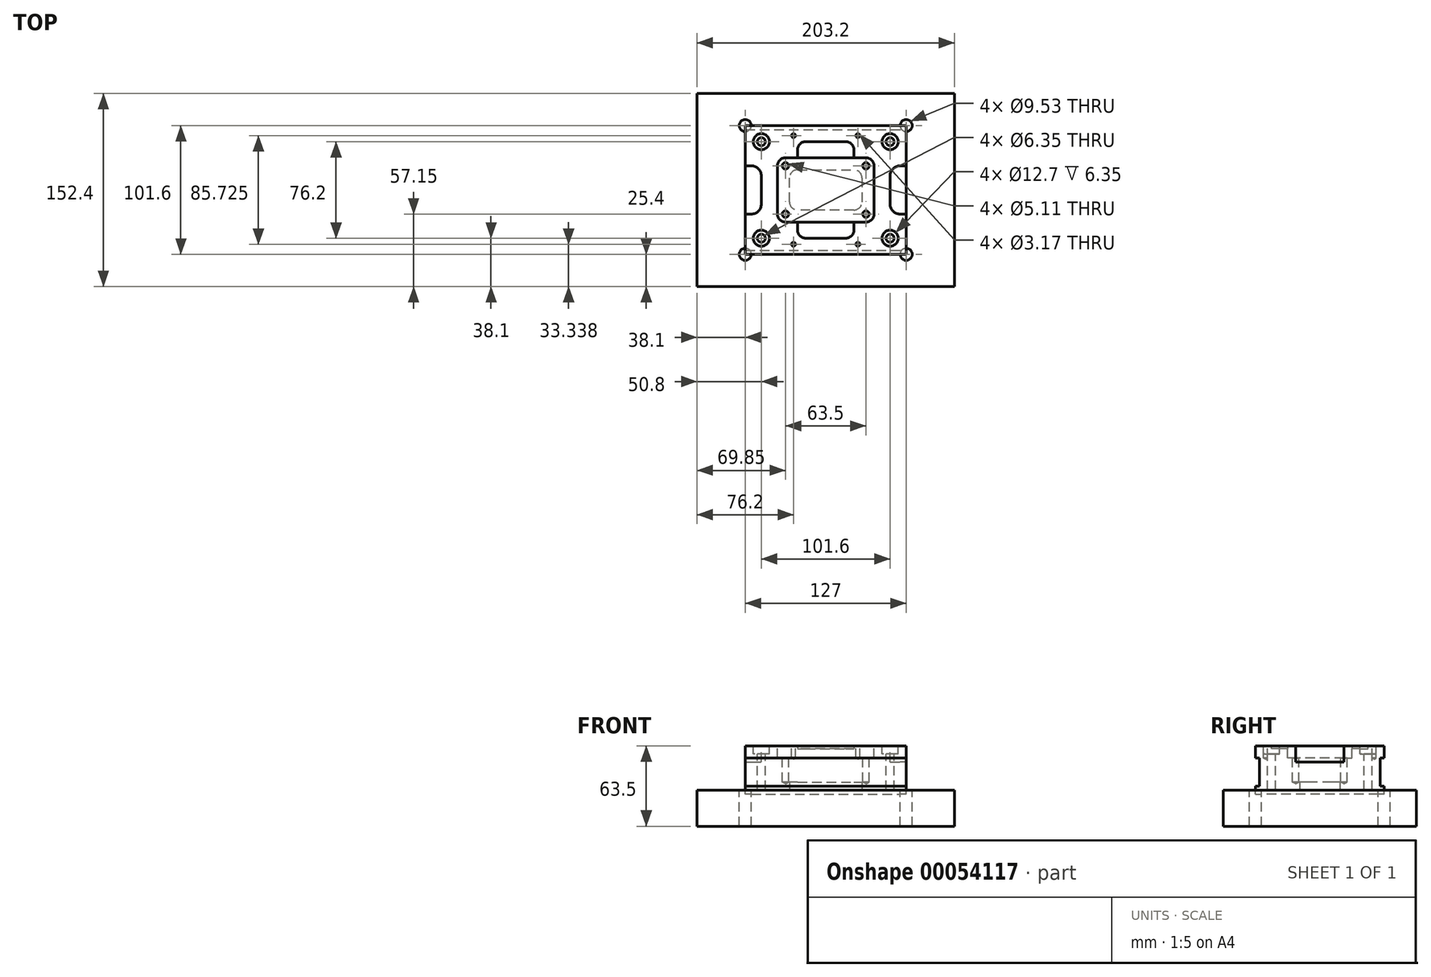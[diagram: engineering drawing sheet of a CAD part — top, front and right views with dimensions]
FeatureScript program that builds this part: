
annotation { "Feature Type Name" : "Feature", "Feature Type Description" : "" }
export const myFeature = defineFeature(function(context is Context, id is Id, definition is map)
    precondition{}
    {
        {
            var Q0;
            Q0=qCreatedBy(makeId("Top.planeOp"),FACE);
            var sketch = newSketch(context, id + "F0", { "sketchPlane" : qUnion([Q0])});
            skLineSegment(sketch, "E0.rect.bottom", {"start": v(-63.5, 50.8) * mm, "end": v(63.5, 50.8) * mm});
            skLineSegment(sketch, "E0.rect.top", {"start": v(-63.5, -50.8) * mm, "end": v(63.5, -50.8) * mm});
            skLineSegment(sketch, "E0.rect.left", {"start": v(-63.5, 50.8) * mm, "end": v(-63.5, -50.8) * mm});
            skLineSegment(sketch, "E0.rect.right", {"start": v(63.5, 50.8) * mm, "end": v(63.5, -50.8) * mm});
            skPoint(sketch, "E0.rect.middle", {"position": v(0, 0) * mm});
            skSolve(sketch);
        }
        {
            var Q0;
            Q0=makeQuery(id+"F0.imprint","IMPRINT",FACE,{"disambiguationData":[TD([[makeQuery(id+"F0.imprint","IMPRINT",EDGE,{"derivedFrom":sQuery(id+"F0.wireOp",EDGE,"E0.rect.bottom")}),-1.0]])]});
            extrude(context, id + "F1", {"entities" : qUnion([Q0]), "depth" : 38.1 * mm});
        }
        {
            var Q0;
            Q0=makeQuery(id+"F1.opExtrude","CAP_FACE",FACE,{"disambiguationData":[OSD([sQuery(id+"F0.wireOp",EDGE,"E0.rect.bottom"),sQuery(id+"F0.wireOp",EDGE,"E0.rect.top"),sQuery(id+"F0.wireOp",EDGE,"E0.rect.left"),sQuery(id+"F0.wireOp",EDGE,"E0.rect.right")])],"isStart":false});
            var sketch = newSketch(context, id + "F2", { "sketchPlane" : qUnion([Q0])});
            skLineSegment(sketch, "E1.rect.bottom", {"start": v(-38.1, 25.4) * mm, "end": v(38.1, 25.4) * mm});
            skLineSegment(sketch, "E1.rect.top", {"start": v(-38.1, -25.4) * mm, "end": v(38.1, -25.4) * mm});
            skLineSegment(sketch, "E1.rect.left", {"start": v(-38.1, 25.4) * mm, "end": v(-38.1, -25.4) * mm});
            skLineSegment(sketch, "E1.rect.right", {"start": v(38.1, 25.4) * mm, "end": v(38.1, -25.4) * mm});
            skPoint(sketch, "E1.rect.middle", {"position": v(0, 0) * mm});
            skSolve(sketch);
        }
        {
            var Q0;
            Q0 = qSketchRegion(id + "F2", true);
            extrude(context, id + "F3", {"entities" : qUnion([Q0]), "operationType" : NewBodyOperationType.REMOVE, "oppositeDirection" : true, "depth" : 9.52 * mm});
        }
        {
            var Q0;
            Q0=makeQuery(id+"F3.boolean.opBoolean","COPY",EDGE,{"derivedFrom":makeQuery(id+"F3.opExtrude","SWEPT_EDGE",EDGE,{"disambiguationData":[OSD([sQuery(id+"F2.wireOp",EDGE,"E1.rect.bottom"),sQuery(id+"F2.wireOp",EDGE,"E1.rect.left")])]})});
            var Q1;
            Q1=makeQuery(id+"F3.boolean.opBoolean","COPY",EDGE,{"derivedFrom":makeQuery(id+"F3.opExtrude","SWEPT_EDGE",EDGE,{"disambiguationData":[OSD([sQuery(id+"F2.wireOp",EDGE,"E1.rect.bottom"),sQuery(id+"F2.wireOp",EDGE,"E1.rect.right")])]})});
            var Q2;
            Q2=makeQuery(id+"F3.boolean.opBoolean","COPY",EDGE,{"derivedFrom":makeQuery(id+"F3.opExtrude","SWEPT_EDGE",EDGE,{"disambiguationData":[OSD([sQuery(id+"F2.wireOp",EDGE,"E1.rect.top"),sQuery(id+"F2.wireOp",EDGE,"E1.rect.right")])]})});
            var Q3;
            Q3=makeQuery(id+"F3.boolean.opBoolean","COPY",EDGE,{"derivedFrom":makeQuery(id+"F3.opExtrude","SWEPT_EDGE",EDGE,{"disambiguationData":[OSD([sQuery(id+"F2.wireOp",EDGE,"E1.rect.top"),sQuery(id+"F2.wireOp",EDGE,"E1.rect.left")])]})});
            fillet(context, id + "F4", {"entities" : qUnion([Q0, Q1, Q2, Q3]), "radius" : 6.35 * mm, "tangentPropagation" : true, "allowEdgeOverflow" : false});
        }
        {
            var Q0;
            Q0=makeQuery(id+"F1.opExtrude","CAP_FACE",FACE,{"disambiguationData":[OSD([sQuery(id+"F0.wireOp",EDGE,"E0.rect.bottom"),sQuery(id+"F0.wireOp",EDGE,"E0.rect.top"),sQuery(id+"F0.wireOp",EDGE,"E0.rect.left"),sQuery(id+"F0.wireOp",EDGE,"E0.rect.right")])],"isStart":false});
            var sketch = newSketch(context, id + "F5", { "sketchPlane" : qUnion([Q0])});
            skPoint(sketch, "E2", {"position": v(50.8, 38.1) * mm});
            skPoint(sketch, "E3", {"position": v(50.8, -38.1) * mm});
            skPoint(sketch, "E4", {"position": v(-50.8, -38.1) * mm});
            skPoint(sketch, "E5", {"position": v(-50.8, 38.1) * mm});
            skSolve(sketch);
        }
        {
            var Q0;
            Q0=sQuery(id+"F5.wireOp",VERTEX,"E5");
            var Q1;
            Q1=sQuery(id+"F5.wireOp",VERTEX,"E2");
            var Q2;
            Q2=sQuery(id+"F5.wireOp",VERTEX,"E3");
            var Q3;
            Q3=sQuery(id+"F5.wireOp",VERTEX,"E4");
            var Q4;
            Q4=makeQuery(id+"F1.opExtrude","SWEPT_BODY",BODY,{"disambiguationData":[OSD([sQuery(id+"F0.wireOp",EDGE,"E0.rect.bottom"),sQuery(id+"F0.wireOp",EDGE,"E0.rect.top"),sQuery(id+"F0.wireOp",EDGE,"E0.rect.left"),sQuery(id+"F0.wireOp",EDGE,"E0.rect.right")])]});
            hole(context, id + "F6", {"style" : HoleStyle.C_BORE, "holeDiameter" : 6.35 * mm, "cBoreDiameter" : 12.7 * mm, "cBoreDepth" : 6.35 * mm, "endStyle" : HoleEndStyle.THROUGH, "locations" : qUnion([Q0, Q1, Q2, Q3]), "scope" : qUnion([Q4])});
        }
        {
            var Q0;
            Q0=makeQuery(id+"F1.opExtrude","SWEPT_FACE",FACE,{"disambiguationData":[OSD([sQuery(id+"F0.wireOp",EDGE,"E0.rect.right")])]});
            var sketch = newSketch(context, id + "F7", { "sketchPlane" : qUnion([Q0])});
            skLineSegment(sketch, "E6.bottom", {"start": v(-50.8, 28.57) * mm, "end": v(-47.62, 28.57) * mm});
            skLineSegment(sketch, "E6.top", {"start": v(-50.8, 6.35) * mm, "end": v(-47.62, 6.35) * mm});
            skLineSegment(sketch, "E6.left", {"start": v(-50.8, 28.57) * mm, "end": v(-50.8, 6.35) * mm});
            skLineSegment(sketch, "E6.right", {"start": v(-47.62, 28.57) * mm, "end": v(-47.62, 6.35) * mm});
            skLineSegment(sketch, "E7.bottom", {"start": v(50.8, 28.57) * mm, "end": v(47.63, 28.57) * mm});
            skLineSegment(sketch, "E7.top", {"start": v(50.8, 6.35) * mm, "end": v(47.63, 6.35) * mm});
            skLineSegment(sketch, "E7.left", {"start": v(50.8, 28.57) * mm, "end": v(50.8, 6.35) * mm});
            skLineSegment(sketch, "E7.right", {"start": v(47.63, 28.58) * mm, "end": v(47.63, 6.35) * mm});
            skSolve(sketch);
        }
        {
            var Q0;
            Q0 = qSketchRegion(id + "F7", true);
            extrude(context, id + "F8", {"entities" : qUnion([Q0]), "operationType" : NewBodyOperationType.REMOVE, "endBound" : BoundingType.THROUGH_ALL, "oppositeDirection" : true, "depth" : 25.4 * mm});
        }
        {
            var Q0;
            Q0=makeQuery(id+"F3.boolean.opBoolean","COPY",FACE,{"derivedFrom":makeQuery(id+"F3.opExtrude","CAP_FACE",FACE,{"disambiguationData":[OSD([sQuery(id+"F2.wireOp",EDGE,"E1.rect.bottom"),sQuery(id+"F2.wireOp",EDGE,"E1.rect.top"),sQuery(id+"F2.wireOp",EDGE,"E1.rect.left"),sQuery(id+"F2.wireOp",EDGE,"E1.rect.right")])],"isStart":false})});
            var sketch = newSketch(context, id + "F9", { "sketchPlane" : qUnion([Q0])});
            skPoint(sketch, "E8", {"position": v(-31.75, 19.05) * mm});
            skPoint(sketch, "E9", {"position": v(-31.75, -19.05) * mm});
            skPoint(sketch, "E10", {"position": v(31.75, 19.05) * mm});
            skPoint(sketch, "E11", {"position": v(31.75, -19.05) * mm});
            skSolve(sketch);
        }
        {
            var Q0;
            Q0=sQuery(id+"F9.wireOp",VERTEX,"E8");
            var Q1;
            Q1=sQuery(id+"F9.wireOp",VERTEX,"E9");
            var Q2;
            Q2=sQuery(id+"F9.wireOp",VERTEX,"E11");
            var Q3;
            Q3=sQuery(id+"F9.wireOp",VERTEX,"E10");
            var Q4;
            Q4=makeQuery(id+"F1.opExtrude","SWEPT_BODY",BODY,{"disambiguationData":[OSD([sQuery(id+"F0.wireOp",EDGE,"E0.rect.bottom"),sQuery(id+"F0.wireOp",EDGE,"E0.rect.top"),sQuery(id+"F0.wireOp",EDGE,"E0.rect.left"),sQuery(id+"F0.wireOp",EDGE,"E0.rect.right")])]});
            hole(context, id + "F10", {"style" : HoleStyle.SIMPLE, "holeDiameter" : 5.1 * mm, "endStyle" : HoleEndStyle.BLIND, "holeDepth" : 19.05 * mm, "locations" : qUnion([Q0, Q1, Q2, Q3]), "scope" : qUnion([Q4])});
        }
        {
            var Q0;
            Q0=makeQuery(id+"F1.opExtrude","CAP_FACE",FACE,{"disambiguationData":[OSD([sQuery(id+"F0.wireOp",EDGE,"E0.rect.bottom"),sQuery(id+"F0.wireOp",EDGE,"E0.rect.top"),sQuery(id+"F0.wireOp",EDGE,"E0.rect.left"),sQuery(id+"F0.wireOp",EDGE,"E0.rect.right")])],"isStart":false});
            var sketch = newSketch(context, id + "F11", { "sketchPlane" : qUnion([Q0])});
            skLineSegment(sketch, "E12.bottom", {"start": v(-63.5, 19.05) * mm, "end": v(-50.8, 19.05) * mm});
            skLineSegment(sketch, "E12.top", {"start": v(-63.5, -19.05) * mm, "end": v(-50.8, -19.05) * mm});
            skLineSegment(sketch, "E12.left", {"start": v(-63.5, 19.05) * mm, "end": v(-63.5, -19.05) * mm});
            skLineSegment(sketch, "E12.right", {"start": v(-50.8, 19.05) * mm, "end": v(-50.8, -19.05) * mm});
            skLineSegment(sketch, "E13.bottom", {"start": v(63.5, 19.05) * mm, "end": v(50.8, 19.05) * mm});
            skLineSegment(sketch, "E13.top", {"start": v(63.5, -19.05) * mm, "end": v(50.8, -19.05) * mm});
            skLineSegment(sketch, "E13.left", {"start": v(63.5, 19.05) * mm, "end": v(63.5, -19.05) * mm});
            skLineSegment(sketch, "E13.right", {"start": v(50.8, 19.05) * mm, "end": v(50.8, -19.05) * mm});
            skSolve(sketch);
        }
        {
            var Q0;
            Q0 = qSketchRegion(id + "F11", true);
            extrude(context, id + "F12", {"entities" : qUnion([Q0]), "operationType" : NewBodyOperationType.REMOVE, "oppositeDirection" : true, "depth" : 12.7 * mm});
        }
        {
            var Q0;
            Q0=makeQuery(id+"F12.boolean.opBoolean","COPY",EDGE,{"derivedFrom":makeQuery(id+"F12.opExtrude","SWEPT_EDGE",EDGE,{"disambiguationData":[OSD([sQuery(id+"F11.wireOp",EDGE,"E12.bottom"),sQuery(id+"F11.wireOp",EDGE,"E12.right")])]})});
            var Q1;
            Q1=makeQuery(id+"F12.boolean.opBoolean","COPY",EDGE,{"derivedFrom":makeQuery(id+"F12.opExtrude","SWEPT_EDGE",EDGE,{"disambiguationData":[OSD([sQuery(id+"F11.wireOp",EDGE,"E12.top"),sQuery(id+"F11.wireOp",EDGE,"E12.right")])]})});
            var Q2;
            Q2=makeQuery(id+"F12.boolean.opBoolean","COPY",EDGE,{"derivedFrom":makeQuery(id+"F12.opExtrude","SWEPT_EDGE",EDGE,{"disambiguationData":[OSD([sQuery(id+"F11.wireOp",EDGE,"E13.bottom"),sQuery(id+"F11.wireOp",EDGE,"E13.right")])]})});
            var Q3;
            Q3=makeQuery(id+"F12.boolean.opBoolean","COPY",EDGE,{"derivedFrom":makeQuery(id+"F12.opExtrude","SWEPT_EDGE",EDGE,{"disambiguationData":[OSD([sQuery(id+"F11.wireOp",EDGE,"E13.top"),sQuery(id+"F11.wireOp",EDGE,"E13.right")])]})});
            fillet(context, id + "F13", {"entities" : qUnion([Q0, Q1, Q2, Q3]), "radius" : 7.94 * mm, "tangentPropagation" : true, "allowEdgeOverflow" : false});
        }
        {
            var Q0;
            Q0=makeQuery(id+"F1.opExtrude","CAP_FACE",FACE,{"disambiguationData":[OSD([sQuery(id+"F0.wireOp",EDGE,"E0.rect.bottom"),sQuery(id+"F0.wireOp",EDGE,"E0.rect.top"),sQuery(id+"F0.wireOp",EDGE,"E0.rect.left"),sQuery(id+"F0.wireOp",EDGE,"E0.rect.right")])],"isStart":true});
            var sketch = newSketch(context, id + "F14", { "sketchPlane" : qUnion([Q0])});
            skLineSegment(sketch, "E14.0.0", {"start": v(31.75, -25.4) * mm, "end": v(-31.75, -25.4) * mm});
            skArc(sketch, "E14.0.1", {"start": v(-31.75, -25.4) * mm, "mid": v(-36.24, -23.54) * mm, "end": v(-38.1, -19.05) * mm});
            skLineSegment(sketch, "E14.0.2", {"start": v(-38.1, -19.05) * mm, "end": v(-38.1, 19.05) * mm});
            skArc(sketch, "E14.0.3", {"start": v(-38.1, 19.05) * mm, "mid": v(-36.24, 23.54) * mm, "end": v(-31.75, 25.4) * mm});
            skLineSegment(sketch, "E14.0.4", {"start": v(-31.75, 25.4) * mm, "end": v(31.75, 25.4) * mm});
            skArc(sketch, "E14.0.5", {"start": v(31.75, 25.4) * mm, "mid": v(36.24, 23.54) * mm, "end": v(38.1, 19.05) * mm});
            skLineSegment(sketch, "E14.0.6", {"start": v(38.1, 19.05) * mm, "end": v(38.1, -19.05) * mm});
            skArc(sketch, "E14.0.7", {"start": v(38.1, -19.05) * mm, "mid": v(36.24, -23.54) * mm, "end": v(31.75, -25.4) * mm});
            skSolve(sketch);
        }
        {
            var Q0;
            Q0 = qSketchRegion(id + "F14", true);
            extrude(context, id + "F15", {"entities" : qUnion([Q0]), "operationType" : NewBodyOperationType.REMOVE, "oppositeDirection" : true, "depth" : 3.17 * mm});
        }
        {
            var Q0;
            Q0=makeQuery(id+"F15.boolean.opBoolean","COPY",FACE,{"derivedFrom":makeQuery(id+"F15.opExtrude","CAP_FACE",FACE,{"disambiguationData":[OSD([sQuery(id+"F14.wireOp",EDGE,"E14.0.0"),sQuery(id+"F14.wireOp",EDGE,"E14.0.1"),sQuery(id+"F14.wireOp",EDGE,"E14.0.2"),sQuery(id+"F14.wireOp",EDGE,"E14.0.3"),sQuery(id+"F14.wireOp",EDGE,"E14.0.4"),sQuery(id+"F14.wireOp",EDGE,"E14.0.5"),sQuery(id+"F14.wireOp",EDGE,"E14.0.6"),sQuery(id+"F14.wireOp",EDGE,"E14.0.7")])],"isStart":false})});
            var sketch = newSketch(context, id + "F16", { "sketchPlane" : qUnion([Q0])});
            skLineSegment(sketch, "E15.0", {"start": v(-28.57, -15.87) * mm, "end": v(28.57, -15.87) * mm});
            skLineSegment(sketch, "E15.1", {"start": v(-28.57, 15.87) * mm, "end": v(-28.57, -15.87) * mm});
            skLineSegment(sketch, "E15.2", {"start": v(28.57, 15.87) * mm, "end": v(-28.57, 15.87) * mm});
            skLineSegment(sketch, "E15.3", {"start": v(28.57, -15.87) * mm, "end": v(28.57, 15.87) * mm});
            skSolve(sketch);
        }
        {
            var Q0;
            Q0 = qSketchRegion(id + "F16", true);
            extrude(context, id + "F17", {"entities" : qUnion([Q0]), "operationType" : NewBodyOperationType.REMOVE, "oppositeDirection" : true, "depth" : 6.35 * mm});
        }
        {
            var Q0;
            Q0=makeQuery(id+"F17.boolean.opBoolean","COPY",EDGE,{"derivedFrom":makeQuery(id+"F17.opExtrude","SWEPT_EDGE",EDGE,{"disambiguationData":[OSD([sQuery(id+"F16.wireOp",EDGE,"E15.1"),sQuery(id+"F16.wireOp",EDGE,"E15.2")])]})});
            var Q1;
            Q1=makeQuery(id+"F17.boolean.opBoolean","COPY",EDGE,{"derivedFrom":makeQuery(id+"F17.opExtrude","SWEPT_EDGE",EDGE,{"disambiguationData":[OSD([sQuery(id+"F16.wireOp",EDGE,"E15.0"),sQuery(id+"F16.wireOp",EDGE,"E15.1")])]})});
            var Q2;
            Q2=makeQuery(id+"F17.boolean.opBoolean","COPY",EDGE,{"derivedFrom":makeQuery(id+"F17.opExtrude","SWEPT_EDGE",EDGE,{"disambiguationData":[OSD([sQuery(id+"F16.wireOp",EDGE,"E15.2"),sQuery(id+"F16.wireOp",EDGE,"E15.3")])]})});
            var Q3;
            Q3=makeQuery(id+"F17.boolean.opBoolean","COPY",EDGE,{"derivedFrom":makeQuery(id+"F17.opExtrude","SWEPT_EDGE",EDGE,{"disambiguationData":[OSD([sQuery(id+"F16.wireOp",EDGE,"E15.0"),sQuery(id+"F16.wireOp",EDGE,"E15.3")])]})});
            fillet(context, id + "F18", {"entities" : qUnion([Q0, Q1, Q2, Q3]), "radius" : 6.35 * mm, "tangentPropagation" : true, "allowEdgeOverflow" : false});
        }
        {
            var Q0;
            Q0=makeQuery(id+"F1.opExtrude","CAP_FACE",FACE,{"disambiguationData":[OSD([sQuery(id+"F0.wireOp",EDGE,"E0.rect.bottom"),sQuery(id+"F0.wireOp",EDGE,"E0.rect.top"),sQuery(id+"F0.wireOp",EDGE,"E0.rect.left"),sQuery(id+"F0.wireOp",EDGE,"E0.rect.right")])],"isStart":false});
            var sketch = newSketch(context, id + "F19", { "sketchPlane" : qUnion([Q0])});
            skPoint(sketch, "E16", {"position": v(-25.4, 42.86) * mm});
            skPoint(sketch, "E17", {"position": v(25.4, 42.86) * mm});
            skPoint(sketch, "E18", {"position": v(-25.4, -42.86) * mm});
            skPoint(sketch, "E19", {"position": v(25.4, -42.86) * mm});
            skSolve(sketch);
        }
        {
            var Q0;
            Q0=sQuery(id+"F19.wireOp",VERTEX,"E16");
            var Q1;
            Q1=sQuery(id+"F19.wireOp",VERTEX,"E17");
            var Q2;
            Q2=sQuery(id+"F19.wireOp",VERTEX,"E18");
            var Q3;
            Q3=sQuery(id+"F19.wireOp",VERTEX,"E19");
            var Q4;
            Q4=makeQuery(id+"F1.opExtrude","SWEPT_BODY",BODY,{"disambiguationData":[OSD([sQuery(id+"F0.wireOp",EDGE,"E0.rect.bottom"),sQuery(id+"F0.wireOp",EDGE,"E0.rect.top"),sQuery(id+"F0.wireOp",EDGE,"E0.rect.left"),sQuery(id+"F0.wireOp",EDGE,"E0.rect.right")])]});
            hole(context, id + "F20", {"style" : HoleStyle.SIMPLE, "holeDiameter" : 3.17 * mm, "endStyle" : HoleEndStyle.BLIND, "holeDepth" : 9.52 * mm, "locations" : qUnion([Q0, Q1, Q2, Q3]), "scope" : qUnion([Q4])});
        }
        {
            var Q0;
            Q0=makeQuery(id+"F1.opExtrude","CAP_FACE",FACE,{"disambiguationData":[OSD([sQuery(id+"F0.wireOp",EDGE,"E0.rect.bottom"),sQuery(id+"F0.wireOp",EDGE,"E0.rect.top"),sQuery(id+"F0.wireOp",EDGE,"E0.rect.left"),sQuery(id+"F0.wireOp",EDGE,"E0.rect.right")])],"isStart":false});
            var sketch = newSketch(context, id + "F21", { "sketchPlane" : qUnion([Q0])});
            skLineSegment(sketch, "E20.bottom", {"start": v(-22.22, 38.1) * mm, "end": v(22.22, 38.1) * mm});
            skLineSegment(sketch, "E20.top", {"start": v(-22.22, -38.1) * mm, "end": v(22.22, -38.1) * mm});
            skLineSegment(sketch, "E20.left", {"start": v(-22.22, 38.1) * mm, "end": v(-22.22, -38.1) * mm});
            skLineSegment(sketch, "E20.right", {"start": v(22.22, 38.1) * mm, "end": v(22.22, -38.1) * mm});
            skSolve(sketch);
        }
        {
            var Q0;
            Q0 = qSketchRegion(id + "F21", true);
            extrude(context, id + "F22", {"entities" : qUnion([Q0]), "operationType" : NewBodyOperationType.REMOVE, "oppositeDirection" : true, "depth" : 2.38 * mm});
        }
        {
            var Q0;
            Q0=makeQuery(id+"F22.boolean.opBoolean","COPY",EDGE,{"derivedFrom":makeQuery(id+"F22.opExtrude","SWEPT_EDGE",EDGE,{"disambiguationData":[OSD([sQuery(id+"F21.wireOp",EDGE,"E20.bottom"),sQuery(id+"F21.wireOp",EDGE,"E20.left")])]})});
            var Q1;
            Q1=makeQuery(id+"F22.boolean.opBoolean","COPY",EDGE,{"derivedFrom":makeQuery(id+"F22.opExtrude","SWEPT_EDGE",EDGE,{"disambiguationData":[OSD([sQuery(id+"F21.wireOp",EDGE,"E20.bottom"),sQuery(id+"F21.wireOp",EDGE,"E20.right")])]})});
            var Q2;
            Q2=makeQuery(id+"F22.boolean.opBoolean","COPY",EDGE,{"derivedFrom":makeQuery(id+"F22.opExtrude","SWEPT_EDGE",EDGE,{"disambiguationData":[OSD([sQuery(id+"F21.wireOp",EDGE,"E20.top"),sQuery(id+"F21.wireOp",EDGE,"E20.right")])]})});
            var Q3;
            Q3=makeQuery(id+"F22.boolean.opBoolean","COPY",EDGE,{"derivedFrom":makeQuery(id+"F22.opExtrude","SWEPT_EDGE",EDGE,{"disambiguationData":[OSD([sQuery(id+"F21.wireOp",EDGE,"E20.top"),sQuery(id+"F21.wireOp",EDGE,"E20.left")])]})});
            fillet(context, id + "F23", {"entities" : qUnion([Q0, Q1, Q2, Q3]), "radius" : 6.35 * mm, "tangentPropagation" : true, "allowEdgeOverflow" : false});
        }
        {
            var Q0;
            Q0=makeQuery(id+"F1.opExtrude","CAP_FACE",FACE,{"disambiguationData":[OSD([sQuery(id+"F0.wireOp",EDGE,"E0.rect.bottom"),sQuery(id+"F0.wireOp",EDGE,"E0.rect.top"),sQuery(id+"F0.wireOp",EDGE,"E0.rect.left"),sQuery(id+"F0.wireOp",EDGE,"E0.rect.right")])],"isStart":true});
            var sketch = newSketch(context, id + "F24", { "sketchPlane" : qUnion([Q0])});
            skLineSegment(sketch, "E21.rect.bottom", {"start": v(-101.6, 76.2) * mm, "end": v(101.6, 76.2) * mm});
            skLineSegment(sketch, "E21.rect.top", {"start": v(-101.6, -76.2) * mm, "end": v(101.6, -76.2) * mm});
            skLineSegment(sketch, "E21.rect.left", {"start": v(-101.6, 76.2) * mm, "end": v(-101.6, -76.2) * mm});
            skLineSegment(sketch, "E21.rect.right", {"start": v(101.6, 76.2) * mm, "end": v(101.6, -76.2) * mm});
            skPoint(sketch, "E21.rect.middle", {"position": v(0, 0) * mm});
            skSolve(sketch);
        }
        {
            var Q0;
            Q0 = qSketchRegion(id + "F24", true);
            extrude(context, id + "F25", {"entities" : qUnion([Q0]), "depth" : 25.4 * mm, "hasSecondDirection" : true, "secondDirectionOppositeDirection" : true, "secondDirectionDepth" : 3.17 * mm});
        }
        {
            var Q0;
            Q0=makeQuery(id+"F25.opExtrude","CAP_FACE",FACE,{"disambiguationData":[OSD([sQuery(id+"F24.wireOp",EDGE,"E21.rect.bottom"),sQuery(id+"F24.wireOp",EDGE,"E21.rect.top"),sQuery(id+"F24.wireOp",EDGE,"E21.rect.left"),sQuery(id+"F24.wireOp",EDGE,"E21.rect.right")])],"isStart":true});
            var sketch = newSketch(context, id + "F26", { "sketchPlane" : qUnion([Q0])});
            skLineSegment(sketch, "E22.bottom", {"start": v(-63.5, 50.8) * mm, "end": v(63.5, 50.8) * mm});
            skLineSegment(sketch, "E22.top", {"start": v(-63.5, -50.8) * mm, "end": v(63.5, -50.8) * mm});
            skLineSegment(sketch, "E22.left", {"start": v(-63.5, 50.8) * mm, "end": v(-63.5, -50.8) * mm});
            skLineSegment(sketch, "E22.right", {"start": v(63.5, 50.8) * mm, "end": v(63.5, -50.8) * mm});
            skSolve(sketch);
        }
        {
            var Q0;
            Q0 = qSketchRegion(id + "F26", true);
            extrude(context, id + "F27", {"entities" : qUnion([Q0]), "operationType" : NewBodyOperationType.REMOVE, "oppositeDirection" : true, "depth" : 3.17 * mm});
        }
        {
            var Q0;
            Q0=makeQuery(id+"F25.opExtrude","CAP_FACE",FACE,{"disambiguationData":[OSD([sQuery(id+"F24.wireOp",EDGE,"E21.rect.bottom"),sQuery(id+"F24.wireOp",EDGE,"E21.rect.top"),sQuery(id+"F24.wireOp",EDGE,"E21.rect.left"),sQuery(id+"F24.wireOp",EDGE,"E21.rect.right")])],"isStart":true});
            var sketch = newSketch(context, id + "F28", { "sketchPlane" : qUnion([Q0])});
            skCircle(sketch, "E23", {"center": v(-63.5, 50.8) * mm, "radius": 4.76 * mm});
            skCircle(sketch, "E24", {"center": v(-63.5, -50.8) * mm, "radius": 4.76 * mm});
            skCircle(sketch, "E25", {"center": v(63.5, 50.8) * mm, "radius": 4.76 * mm});
            skCircle(sketch, "E26", {"center": v(63.5, -50.8) * mm, "radius": 4.76 * mm});
            skSolve(sketch);
        }
        {
            var Q0;
            Q0 = qSketchRegion(id + "F28", true);
            extrude(context, id + "F29", {"entities" : qUnion([Q0]), "operationType" : NewBodyOperationType.REMOVE, "endBound" : BoundingType.THROUGH_ALL, "oppositeDirection" : true, "depth" : 25.4 * mm});
        }
    });
